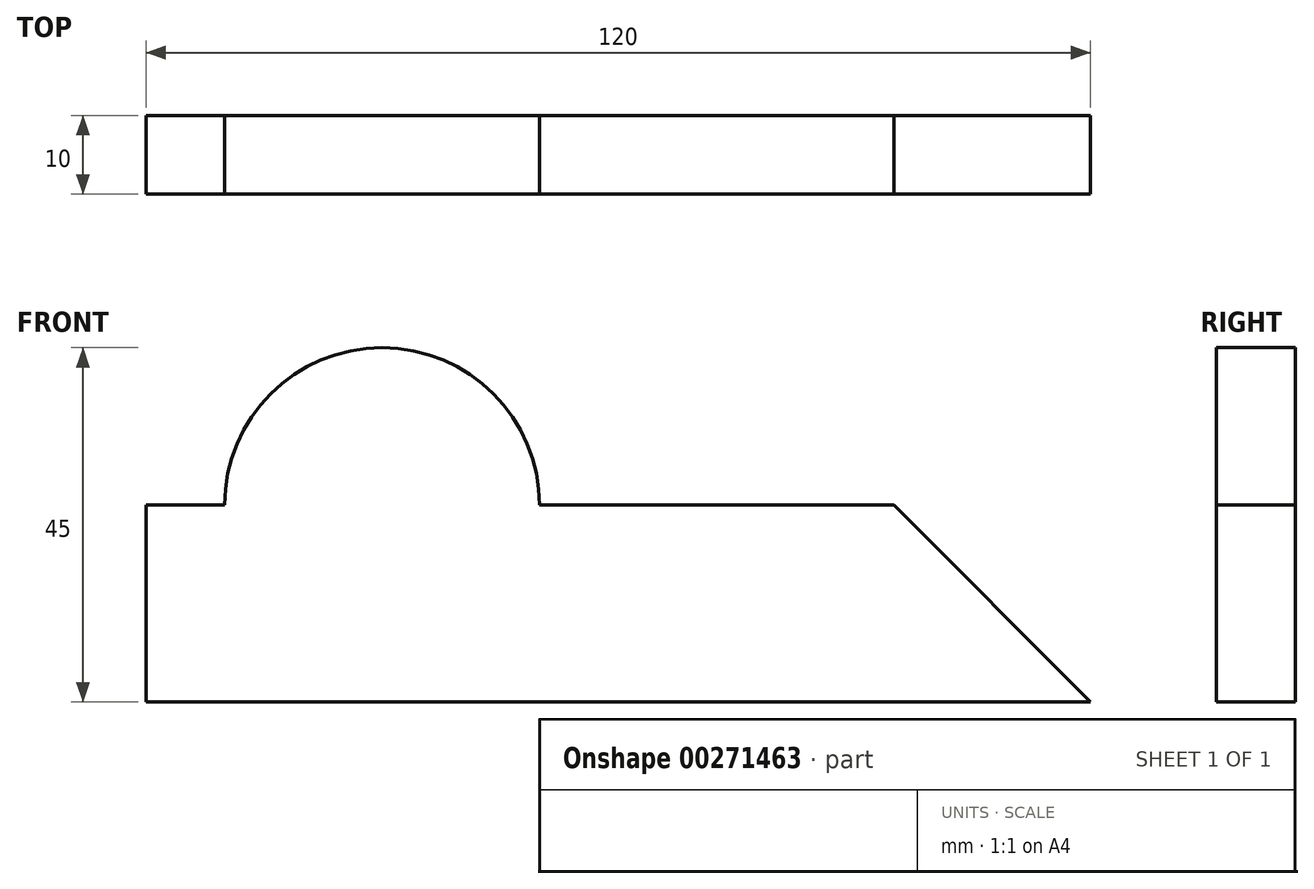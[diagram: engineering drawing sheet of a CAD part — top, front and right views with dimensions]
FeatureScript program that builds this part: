
annotation { "Feature Type Name" : "Feature", "Feature Type Description" : "" }
export const myFeature = defineFeature(function(context is Context, id is Id, definition is map)
    precondition{}
    {
        {
            var Q0;
            Q0=qCreatedBy(makeId("Front.planeOp"),FACE);
            var sketch = newSketch(context, id + "F0", { "sketchPlane" : qUnion([Q0])});
            skLineSegment(sketch, "E0", {"start": v(0, 0) * mm, "end": v(120, 0) * mm});
            skLineSegment(sketch, "E1", {"start": v(120, 0) * mm, "end": v(95, 25) * mm});
            skLineSegment(sketch, "E2", {"start": v(95, 25) * mm, "end": v(50, 25) * mm});
            skLineSegment(sketch, "E3", {"start": v(0, 0) * mm, "end": v(0, 25) * mm});
            skLineSegment(sketch, "E4", {"start": v(0, 25) * mm, "end": v(10, 25) * mm});
            skCircle(sketch, "E5", {"center": v(30, 25) * mm, "radius": 10 * mm});
            skArc(sketch, "E6", {"start": v(50, 25) * mm, "mid": v(30, 45) * mm, "end": v(10, 25) * mm});
            skSolve(sketch);
        }
        {
            var Q0;
            Q0=makeQuery(id+"F0.imprint","IMPRINT",FACE,{"disambiguationData":[TD([[makeQuery(id+"F0.imprint","IMPRINT",EDGE,{"derivedFrom":sQuery(id+"F0.wireOp",EDGE,"E5")}),1.0]])]});
            var Q1;
            Q1=makeQuery(id+"F0.imprint","IMPRINT",FACE,{"disambiguationData":[TD([[makeQuery(id+"F0.imprint","IMPRINT",EDGE,{"derivedFrom":sQuery(id+"F0.wireOp",EDGE,"E0")}),1.0]])]});
            extrude(context, id + "F1", {"entities" : qUnion([Q0, Q1]), "depth" : 10 * mm});
        }
    });
